# Revit family: IS_ConnectAir_E0042_BIM_DE
name_source: partatom
category: Plumbing Fixtures
revit_build: Autodesk Revit MEP 2014 (Build: 20130308_1515(x64)
units: mm (PartAtom-declared; Revit-internal decimal feet)

## types (4) — shared parameters
Accessories = www.idealstandard.de\ersatzteile
AreaUnits = millimeters
Assembly Code = C1030200
AssetType = Fixed
Brand = Ideal Standard
CodePerformance = DIN EN 997 CL1 - 6A/5A DIN EN 33
ConnectionType = Plumbing
DurationUnit = year
ExpectedLife = 25
Features = Connect Air back-to-wall bowl, wash-down, AquaBlade
GrossWeight = 0
IfcExportAs = IfcSanitaryTerminalType
IfcExportType = TOILETPAN
InstallationInstructions = www.idealstandard.de\produkte
LinearUnits = millimeters
ManufacturerURL = www.idealstandard.com
NBSDescription = WC pans
NBSReference = 45-30-70/384
NettWeight = 25 kg
NominalHeight = 400 mm  [stored 1.31234 ft]
NominalLength = 549 mm
NominalWidth = 364 mm
PanColor = White
PanMaterial = Vitreous china
PanMounting = BackToWall
ProductInformation = www.idealstandard.de/produkte
Shape = Sculptured
Size = 360x545x400mm
Space = Internal
ToiletPanType = WashDown
ToiletType = Other
URL = www.idealstandard.com
Uniclass2015Code = Pr_40_20_93_94
Uniclass2015Title = WC pans
Uniclass2015Version = Products v1.1
Version = 1
VolumeUnits = Litres
WarrantyDescription = Manufacturers Warranty
WarrantyDurationUnit = year
zero-valued in all types: CWFU, Cost, Default Elevation, HWFU, SpilloverLevel, WFU

## per-type parameters (varying)
| type | BIMObjectName | BarCode | Description | E0365,E0366 | E0367,E0368 | Finish | Model | ModelNumber | ModelReference | Name |
| E004201 - Connect Air back-to-wall bowl, wash-down, AquaBlade(E0365,E0366) | ISI_IdealStandard_WcPans_ConnectAir_E004201 | 5017830514084 | E004201 Connect Air back-to-wall bowl, wash-down, AquaBlade | Yes | No | white | E004201 | E004201 | E004201 Connect Air back-to-wall bowl, wash-down, AquaBlade | WcPans_ConnectAir_E004201_IdealStandard |
| E0042MA - Connect Air back-to-wall bowl, wash-down, AquaBlade(E0365,E0366) | ISI_IdealStandard_WcPans_ConnectAir_E0042MA | 5017830518259 | E0042MA Connect Air back-to-wall bowl, wash-down, AquaBlade | Yes | No | white with ideal plus | E0042MA | E0042MA | E0042MA Connect Air back-to-wall bowl, wash-down, AquaBlade | WcPans_ConnectAir_E0042MA_IdealStandard |
| E004201 - Connect Air back-to-wall bowl, wash-down, AquaBlade(E0367,E0368) | ISI_IdealStandard_WcPans_ConnectAir_E004201 | 5017830514084 | E004201 Connect Air back-to-wall bowl, wash-down, AquaBlade | No | Yes | white | E004201 | E004201 | E004201 Connect Air back-to-wall bowl, wash-down, AquaBlade | WcPans_ConnectAir_E004201_IdealStandard |
| E0042MA - Connect Air back-to-wall bowl, wash-down, AquaBlade(E0367,E0368) | ISI_IdealStandard_WcPans_ConnectAir_E0042MA | 5017830518259 | E0042MA Connect Air back-to-wall bowl, wash-down, AquaBlade | No | Yes | white with ideal plus | E0042MA | E0042MA | E0042MA Connect Air back-to-wall bowl, wash-down, AquaBlade | WcPans_ConnectAir_E0042MA_IdealStandard |

note: [stored X ft] marks values corroborated as IEEE doubles in the binary element streams (Revit-internal decimal feet)

## geometry (parser evidence)
native form markers: Sweep x4
no freeform markers — native parametric forms only
